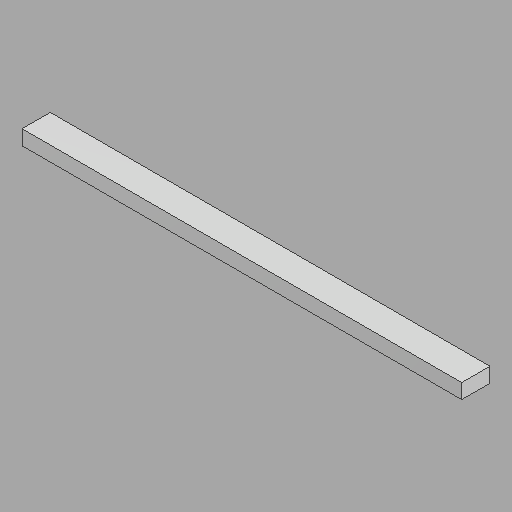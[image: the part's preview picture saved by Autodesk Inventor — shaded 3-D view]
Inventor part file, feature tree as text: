
AUTODESK INVENTOR PART (.ipt)
format: ipt  version: 2022.2 (Build 262287010, 287A)  size: 112,128 bytes
history: native  units: in
note: dims shown in document units (in); Inventor stores cm internally (conversion verified against a paired STEP export)
features: direct_edit x1, other x1, revolve x1
ambient origin geometry x8: Origin, YZ Plane, XZ Plane, XY Plane, X Axis, Y Axis, Z Axis, Center Point
bodies: Solid1 (feature_tree)
feature tree (3):
  direct_edit  "Direct Edit1"
  other  "Head (L)"
  revolve  "Rotate1"  Angle=90.0deg
